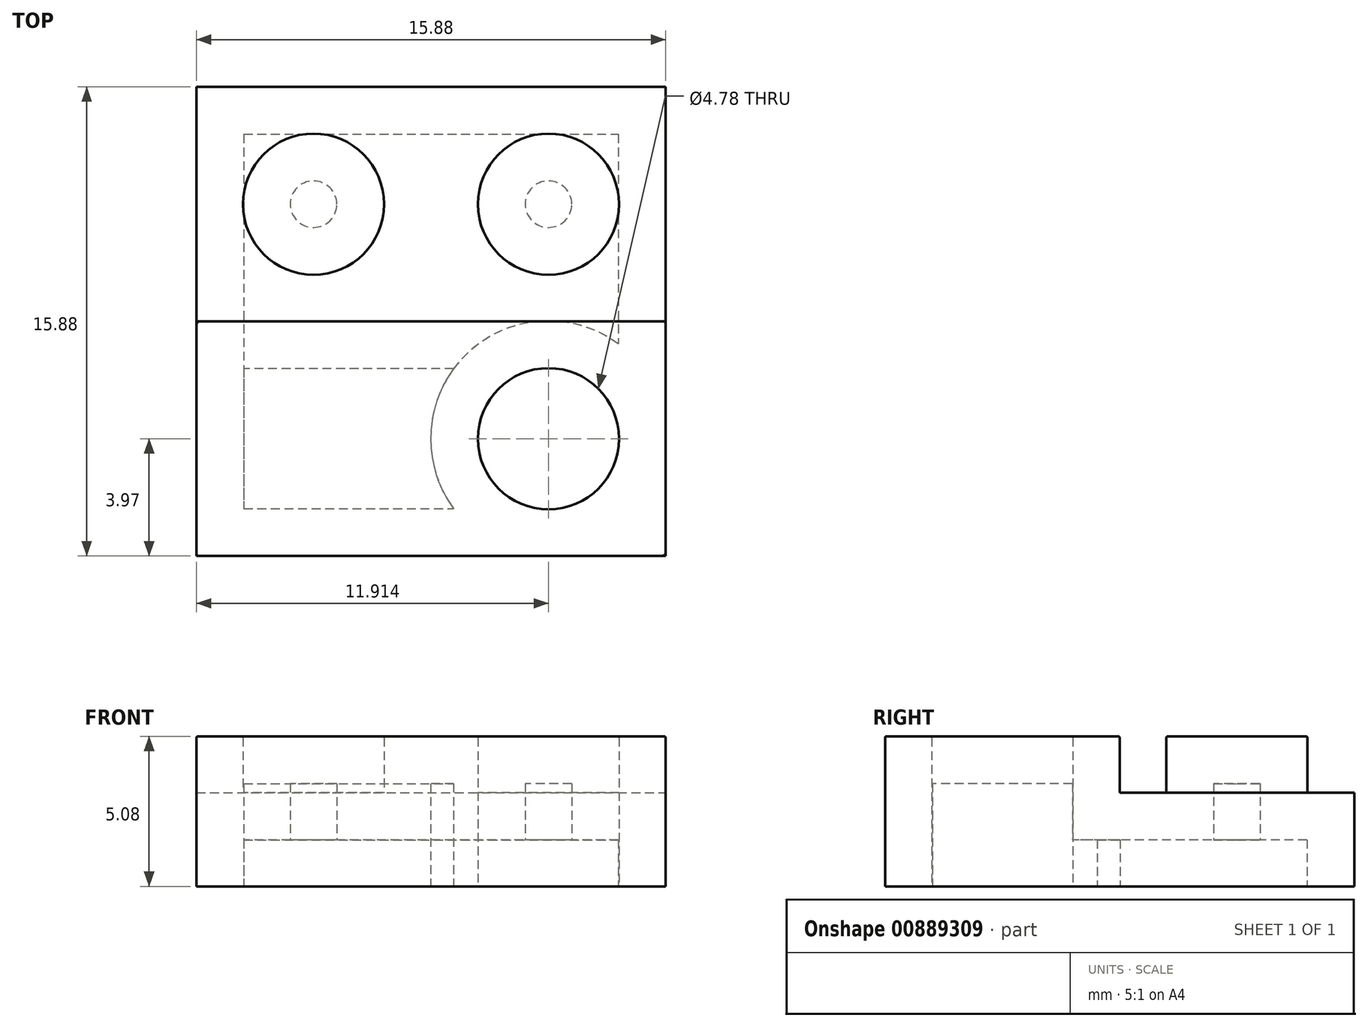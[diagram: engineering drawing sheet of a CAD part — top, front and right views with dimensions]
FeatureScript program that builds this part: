
annotation { "Feature Type Name" : "Feature", "Feature Type Description" : "" }
export const myFeature = defineFeature(function(context is Context, id is Id, definition is map)
    precondition{}
    {
        {
            var Q0;
            Q0=qCreatedBy(makeId("Top.planeOp"),FACE);
            var sketch = newSketch(context, id + "F0", { "sketchPlane" : qUnion([Q0])});
            skLineSegment(sketch, "E0.bottom", {"start": v(-38.8, 8.6) * mm, "end": v(-22.93, 8.6) * mm});
            skLineSegment(sketch, "E0.top", {"start": v(-38.8, -7.28) * mm, "end": v(-22.93, -7.28) * mm});
            skLineSegment(sketch, "E0.left", {"start": v(-38.8, 8.6) * mm, "end": v(-38.8, -7.28) * mm});
            skLineSegment(sketch, "E0.right", {"start": v(-22.93, 8.6) * mm, "end": v(-22.93, -7.28) * mm});
            skLineSegment(sketch, "E1", {"start": v(-38.8, 0.66) * mm, "end": v(-22.93, 0.66) * mm});
            skLineSegment(sketch, "E2", {"start": v(-22.93, 8.6) * mm, "end": v(-22.93, 0.66) * mm});
            skLineSegment(sketch, "E3", {"start": v(-22.93, 0.66) * mm, "end": v(-22.93, -7.28) * mm});
            skLineSegment(sketch, "E4", {"start": v(-38.8, 8.6) * mm, "end": v(-38.8, 0.66) * mm});
            skLineSegment(sketch, "E5", {"start": v(-38.8, -7.28) * mm, "end": v(-38.8, 0.66) * mm});
            skLineSegment(sketch, "E6", {"start": v(-22.93, -3.31) * mm, "end": v(-38.8, -3.31) * mm});
            skLineSegment(sketch, "E7", {"start": v(-38.8, -3.31) * mm, "end": v(-38.8, 4.63) * mm});
            skLineSegment(sketch, "E8", {"start": v(-38.8, 4.63) * mm, "end": v(-22.93, 4.63) * mm});
            skCircle(sketch, "E9", {"center": v(-34.85, 4.63) * mm, "radius": 2.39 * mm});
            skCircle(sketch, "E10.1.0.0", {"center": v(-26.9, 4.63) * mm, "radius": 2.39 * mm});
            skLineSegment(sketch, "E10.direction1", {"start": v(-34.85, 4.63) * mm, "end": v(-26.9, 4.63) * mm, "construction": true});
            skCircle(sketch, "E11.MirrorC", {"center": v(-34.85, -3.31) * mm, "radius": 2.39 * mm});
            skCircle(sketch, "E12.MirrorC", {"center": v(-26.9, -3.31) * mm, "radius": 2.39 * mm});
            skSolve(sketch);
        }
        {
            var Q0;
            {var subQ8=sQuery(id+"F0.wireOp",EDGE,"E0.bottom");Q0=makeQuery(id+"F0.imprint","IMPRINT",FACE,{"disambiguationData":[TD([[makeQuery(id+"F0.imprint","IMPRINT",EDGE,{"derivedFrom":subQ8}),-1.0]])]});}
            var Q1;
            {var subQ12=sQuery(id+"F0.wireOp",EDGE,"E1");Q1=makeQuery(id+"F0.imprint","IMPRINT",FACE,{"disambiguationData":[TD([[makeQuery(id+"F0.imprint","IMPRINT",EDGE,{"derivedFrom":subQ12}),1.0]])]});}
            var Q2;
            {var subQ12=sQuery(id+"F0.wireOp",EDGE,"E0.top");Q2=makeQuery(id+"F0.imprint","IMPRINT",FACE,{"disambiguationData":[TD([[makeQuery(id+"F0.imprint","IMPRINT",EDGE,{"derivedFrom":subQ12}),1.0]])]});}
            var Q3;
            {var subQ8=sQuery(id+"F0.wireOp",EDGE,"E1");Q3=makeQuery(id+"F0.imprint","IMPRINT",FACE,{"disambiguationData":[TD([[makeQuery(id+"F0.imprint","IMPRINT",EDGE,{"derivedFrom":subQ8}),-1.0]])]});}
            extrude(context, id + "F1", {"entities" : qUnion([Q0, Q1, Q2, Q3]), "depth" : 3.17 * mm, "offsetDistance" : 25.4 * mm});
        }
        {
            var Q0;
            {var subQ0=sQuery(id+"F0.wireOp",EDGE,"E9");var subQ1=sQuery(id+"F0.wireOp",EDGE,"E8");var subQ2=makeQuery(id+"F0.imprint","INTERSECT",VERTEX,{"disambiguationData":[OD(0.0)],"derivedFrom":[subQ1,subQ0]});Q0=makeQuery(id+"F0.imprint","IMPRINT",FACE,{"disambiguationData":[TD([[makeQuery(id+"F0.imprint","IMPRINT",EDGE,{"disambiguationData":[TD([[subQ2,-1.0]])],"derivedFrom":subQ1}),-1.0]])]});}
            var Q1;
            {var subQ0=sQuery(id+"F0.wireOp",EDGE,"E9");var subQ1=sQuery(id+"F0.wireOp",EDGE,"E8");var subQ2=makeQuery(id+"F0.imprint","INTERSECT",VERTEX,{"disambiguationData":[OD(0.0)],"derivedFrom":[subQ1,subQ0]});Q1=makeQuery(id+"F0.imprint","IMPRINT",FACE,{"disambiguationData":[TD([[makeQuery(id+"F0.imprint","IMPRINT",EDGE,{"disambiguationData":[TD([[subQ2,-1.0]])],"derivedFrom":subQ1}),1.0]])]});}
            var Q2;
            {var subQ0=sQuery(id+"F0.wireOp",EDGE,"E11.MirrorC");var subQ1=sQuery(id+"F0.wireOp",EDGE,"E6");var subQ2=makeQuery(id+"F0.imprint","INTERSECT",VERTEX,{"disambiguationData":[OD(0.0)],"derivedFrom":[subQ1,subQ0]});Q2=makeQuery(id+"F0.imprint","IMPRINT",FACE,{"disambiguationData":[TD([[makeQuery(id+"F0.imprint","IMPRINT",EDGE,{"disambiguationData":[TD([[subQ2,-1.0]])],"derivedFrom":subQ1}),-1.0]])]});}
            var Q3;
            {var subQ0=sQuery(id+"F0.wireOp",EDGE,"E11.MirrorC");var subQ1=sQuery(id+"F0.wireOp",EDGE,"E6");var subQ2=makeQuery(id+"F0.imprint","INTERSECT",VERTEX,{"disambiguationData":[OD(0.0)],"derivedFrom":[subQ1,subQ0]});Q3=makeQuery(id+"F0.imprint","IMPRINT",FACE,{"disambiguationData":[TD([[makeQuery(id+"F0.imprint","IMPRINT",EDGE,{"disambiguationData":[TD([[subQ2,-1.0]])],"derivedFrom":subQ1}),1.0]])]});}
            var Q4;
            {var subQ0=sQuery(id+"F0.wireOp",EDGE,"E12.MirrorC");var subQ1=sQuery(id+"F0.wireOp",EDGE,"E6");var subQ2=makeQuery(id+"F0.imprint","INTERSECT",VERTEX,{"disambiguationData":[OD(0.0)],"derivedFrom":[subQ1,subQ0]});Q4=makeQuery(id+"F0.imprint","IMPRINT",FACE,{"disambiguationData":[TD([[makeQuery(id+"F0.imprint","IMPRINT",EDGE,{"disambiguationData":[TD([[subQ2,-1.0]])],"derivedFrom":subQ1}),1.0]])]});}
            var Q5;
            {var subQ0=sQuery(id+"F0.wireOp",EDGE,"E12.MirrorC");var subQ1=sQuery(id+"F0.wireOp",EDGE,"E6");var subQ2=makeQuery(id+"F0.imprint","INTERSECT",VERTEX,{"disambiguationData":[OD(0.0)],"derivedFrom":[subQ1,subQ0]});Q5=makeQuery(id+"F0.imprint","IMPRINT",FACE,{"disambiguationData":[TD([[makeQuery(id+"F0.imprint","IMPRINT",EDGE,{"disambiguationData":[TD([[subQ2,-1.0]])],"derivedFrom":subQ1}),-1.0]])]});}
            var Q6;
            {var subQ0=sQuery(id+"F0.wireOp",EDGE,"E10.1.0.0");var subQ1=sQuery(id+"F0.wireOp",EDGE,"E8");var subQ2=makeQuery(id+"F0.imprint","INTERSECT",VERTEX,{"disambiguationData":[OD(0.0)],"derivedFrom":[subQ1,subQ0]});Q6=makeQuery(id+"F0.imprint","IMPRINT",FACE,{"disambiguationData":[TD([[makeQuery(id+"F0.imprint","IMPRINT",EDGE,{"disambiguationData":[TD([[subQ2,-1.0]])],"derivedFrom":subQ1}),-1.0]])]});}
            var Q7;
            {var subQ0=sQuery(id+"F0.wireOp",EDGE,"E10.1.0.0");var subQ1=sQuery(id+"F0.wireOp",EDGE,"E8");var subQ2=makeQuery(id+"F0.imprint","INTERSECT",VERTEX,{"disambiguationData":[OD(0.0)],"derivedFrom":[subQ1,subQ0]});Q7=makeQuery(id+"F0.imprint","IMPRINT",FACE,{"disambiguationData":[TD([[makeQuery(id+"F0.imprint","IMPRINT",EDGE,{"disambiguationData":[TD([[subQ2,-1.0]])],"derivedFrom":subQ1}),1.0]])]});}
            var Q8;
            {var subQ0=sQuery(id+"F0.wireOp",EDGE,"772b9b9a-57aa-4227-97b4-834604aea7ab0.MirrorC");var subQ1=sQuery(id+"F0.wireOp",EDGE,"E6");var subQ2=makeQuery(id+"F0.imprint","INTERSECT",VERTEX,{"disambiguationData":[OD(0.0)],"derivedFrom":[subQ1,subQ0]});Q8=makeQuery(id+"F0.imprint","IMPRINT",FACE,{"disambiguationData":[TD([[makeQuery(id+"F0.imprint","IMPRINT",EDGE,{"disambiguationData":[TD([[subQ2,-1.0]])],"derivedFrom":subQ1}),1.0]])]});}
            var Q9;
            {var subQ0=sQuery(id+"F0.wireOp",EDGE,"772b9b9a-57aa-4227-97b4-834604aea7ab0.MirrorC");var subQ1=sQuery(id+"F0.wireOp",EDGE,"E6");var subQ2=makeQuery(id+"F0.imprint","INTERSECT",VERTEX,{"disambiguationData":[OD(0.0)],"derivedFrom":[subQ1,subQ0]});Q9=makeQuery(id+"F0.imprint","IMPRINT",FACE,{"disambiguationData":[TD([[makeQuery(id+"F0.imprint","IMPRINT",EDGE,{"disambiguationData":[TD([[subQ2,-1.0]])],"derivedFrom":subQ1}),-1.0]])]});}
            var Q10;
            {var subQ0=sQuery(id+"F0.wireOp",EDGE,"E10.2.0.0");var subQ1=sQuery(id+"F0.wireOp",EDGE,"E8");var subQ2=makeQuery(id+"F0.imprint","INTERSECT",VERTEX,{"disambiguationData":[OD(0.0)],"derivedFrom":[subQ1,subQ0]});Q10=makeQuery(id+"F0.imprint","IMPRINT",FACE,{"disambiguationData":[TD([[makeQuery(id+"F0.imprint","IMPRINT",EDGE,{"disambiguationData":[TD([[subQ2,-1.0]])],"derivedFrom":subQ1}),1.0]])]});}
            var Q11;
            {var subQ0=sQuery(id+"F0.wireOp",EDGE,"E10.2.0.0");var subQ1=sQuery(id+"F0.wireOp",EDGE,"E8");var subQ2=makeQuery(id+"F0.imprint","INTERSECT",VERTEX,{"disambiguationData":[OD(0.0)],"derivedFrom":[subQ1,subQ0]});Q11=makeQuery(id+"F0.imprint","IMPRINT",FACE,{"disambiguationData":[TD([[makeQuery(id+"F0.imprint","IMPRINT",EDGE,{"disambiguationData":[TD([[subQ2,-1.0]])],"derivedFrom":subQ1}),-1.0]])]});}
            var Q12;
            {var subQ0=sQuery(id+"F0.wireOp",EDGE,"e7604e88-3f8e-44a0-a98f-2b40e970379b0.MirrorC");var subQ1=sQuery(id+"F0.wireOp",EDGE,"E6");var subQ2=makeQuery(id+"F0.imprint","INTERSECT",VERTEX,{"disambiguationData":[OD(0.0)],"derivedFrom":[subQ1,subQ0]});Q12=makeQuery(id+"F0.imprint","IMPRINT",FACE,{"disambiguationData":[TD([[makeQuery(id+"F0.imprint","IMPRINT",EDGE,{"disambiguationData":[TD([[subQ2,-1.0]])],"derivedFrom":subQ1}),-1.0]])]});}
            var Q13;
            {var subQ0=sQuery(id+"F0.wireOp",EDGE,"e7604e88-3f8e-44a0-a98f-2b40e970379b0.MirrorC");var subQ1=sQuery(id+"F0.wireOp",EDGE,"E6");var subQ2=makeQuery(id+"F0.imprint","INTERSECT",VERTEX,{"disambiguationData":[OD(0.0)],"derivedFrom":[subQ1,subQ0]});Q13=makeQuery(id+"F0.imprint","IMPRINT",FACE,{"disambiguationData":[TD([[makeQuery(id+"F0.imprint","IMPRINT",EDGE,{"disambiguationData":[TD([[subQ2,-1.0]])],"derivedFrom":subQ1}),1.0]])]});}
            var Q14;
            {var subQ0=sQuery(id+"F0.wireOp",EDGE,"E10.3.0.0");var subQ1=sQuery(id+"F0.wireOp",EDGE,"E8");var subQ2=makeQuery(id+"F0.imprint","INTERSECT",VERTEX,{"disambiguationData":[OD(0.0)],"derivedFrom":[subQ1,subQ0]});Q14=makeQuery(id+"F0.imprint","IMPRINT",FACE,{"disambiguationData":[TD([[makeQuery(id+"F0.imprint","IMPRINT",EDGE,{"disambiguationData":[TD([[subQ2,-1.0]])],"derivedFrom":subQ1}),-1.0]])]});}
            var Q15;
            {var subQ0=sQuery(id+"F0.wireOp",EDGE,"E10.3.0.0");var subQ1=sQuery(id+"F0.wireOp",EDGE,"E8");var subQ2=makeQuery(id+"F0.imprint","INTERSECT",VERTEX,{"disambiguationData":[OD(0.0)],"derivedFrom":[subQ1,subQ0]});Q15=makeQuery(id+"F0.imprint","IMPRINT",FACE,{"disambiguationData":[TD([[makeQuery(id+"F0.imprint","IMPRINT",EDGE,{"disambiguationData":[TD([[subQ2,-1.0]])],"derivedFrom":subQ1}),1.0]])]});}
            var Q16;
            Q16=qSketchRegion(id+"FatHljnlFBaRiWF_0",true);
            extrude(context, id + "F2", {"entities" : qUnion([Q0, Q1, Q2, Q3, Q4, Q5, Q6, Q7, Q8, Q9, Q10, Q11, Q12, Q13, Q14, Q15, Q16]), "operationType" : NewBodyOperationType.ADD, "depth" : 5.08 * mm, "offsetDistance" : 25.4 * mm});
        }
        {
            var Q0;
            {var subQ0=sQuery(id+"F0.wireOp",EDGE,"e7604e88-3f8e-44a0-a98f-2b40e970379b0.MirrorC");var subQ1=sQuery(id+"F0.wireOp",EDGE,"772b9b9a-57aa-4227-97b4-834604aea7ab0.MirrorC");var subQ2=sQuery(id+"F0.wireOp",EDGE,"E12.MirrorC");var subQ3=sQuery(id+"F0.wireOp",EDGE,"E11.MirrorC");var subQ4=sQuery(id+"F0.wireOp",EDGE,"E10.3.0.0");var subQ5=sQuery(id+"F0.wireOp",EDGE,"E10.2.0.0");var subQ6=sQuery(id+"F0.wireOp",EDGE,"E10.1.0.0");var subQ7=sQuery(id+"F0.wireOp",EDGE,"E9");Q0=makeQuery(id+"F2.boolean.opBoolean","MERGE",FACE,{"derivedFrom":[makeQuery(id+"F1.opExtrude","CAP_FACE",FACE,{"disambiguationData":[OSD([sQuery(id+"F0.wireOp",EDGE,"E0.bottom"),sQuery(id+"F0.wireOp",EDGE,"E0.top"),sQuery(id+"F0.wireOp",EDGE,"E2"),sQuery(id+"F0.wireOp",EDGE,"E3"),sQuery(id+"F0.wireOp",EDGE,"E4"),sQuery(id+"F0.wireOp",EDGE,"E5"),sQuery(id+"F0.wireOp",EDGE,"E7"),subQ7,subQ6,subQ5,subQ4,subQ3,subQ2,subQ1,subQ0])],"isStart":true}),makeQuery(id+"F2.opExtrude","CAP_FACE",FACE,{"disambiguationData":[OSD([subQ7])],"isStart":true}),makeQuery(id+"F2.opExtrude","CAP_FACE",FACE,{"disambiguationData":[OSD([subQ6])],"isStart":true}),makeQuery(id+"F2.opExtrude","CAP_FACE",FACE,{"disambiguationData":[OSD([subQ5])],"isStart":true}),makeQuery(id+"F2.opExtrude","CAP_FACE",FACE,{"disambiguationData":[OSD([subQ4])],"isStart":true}),makeQuery(id+"F2.opExtrude","CAP_FACE",FACE,{"disambiguationData":[OSD([subQ3])],"isStart":true}),makeQuery(id+"F2.opExtrude","CAP_FACE",FACE,{"disambiguationData":[OSD([subQ2])],"isStart":true}),makeQuery(id+"F2.opExtrude","CAP_FACE",FACE,{"disambiguationData":[OSD([subQ1])],"isStart":true}),makeQuery(id+"F2.opExtrude","CAP_FACE",FACE,{"disambiguationData":[OSD([subQ0])],"isStart":true})]});}
            shell(context, id + "F3", {"entities" : qUnion([Q0]), "thickness" : 1.6 * mm});
        }
        {
            var Q0;
            Q0=makeQuery(id+"F2.opExtrude","CAP_FACE",FACE,{"disambiguationData":[OSD([sQuery(id+"F0.wireOp",EDGE,"E11.MirrorC")])],"isStart":false});
            var Q1;
            Q1=makeQuery(id+"F2.opExtrude","CAP_FACE",FACE,{"disambiguationData":[OSD([sQuery(id+"F0.wireOp",EDGE,"E12.MirrorC")])],"isStart":false});
            var Q2;
            Q2=makeQuery(id+"F2.opExtrude","CAP_FACE",FACE,{"disambiguationData":[OSD([sQuery(id+"F0.wireOp",EDGE,"E10.1.0.0")])],"isStart":false});
            var Q3;
            Q3=makeQuery(id+"F2.opExtrude","CAP_FACE",FACE,{"disambiguationData":[OSD([sQuery(id+"F0.wireOp",EDGE,"E9")])],"isStart":false});
            fillet(context, id + "F4", {"entities" : qUnion([Q0, Q1, Q2, Q3]), "radius" : 0.05 * mm, "tangentPropagation" : true, "allowEdgeOverflow" : false});
        }
    });
